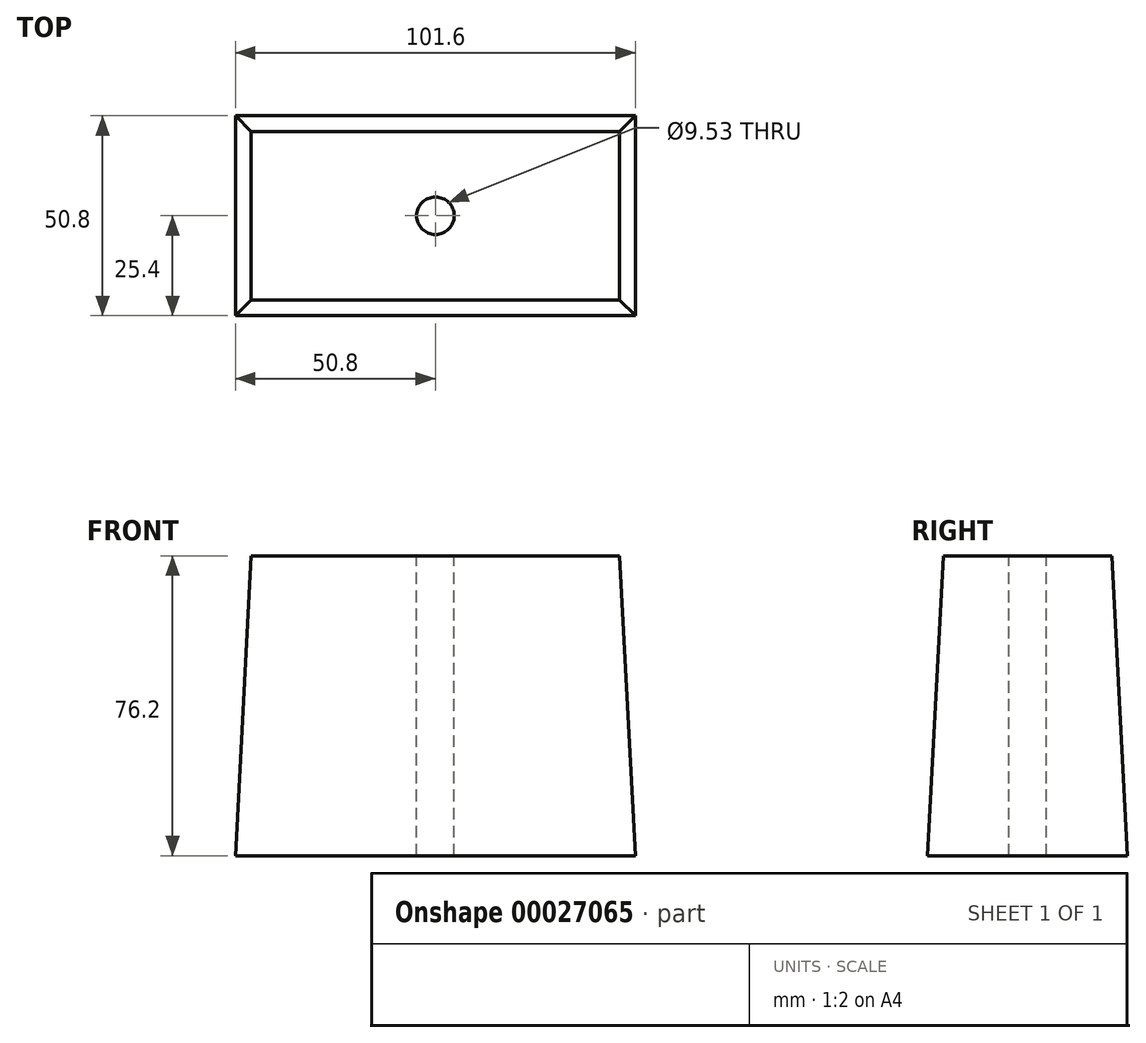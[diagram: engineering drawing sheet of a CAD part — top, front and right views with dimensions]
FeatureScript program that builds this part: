
annotation { "Feature Type Name" : "Feature", "Feature Type Description" : "" }
export const myFeature = defineFeature(function(context is Context, id is Id, definition is map)
    precondition{}
    {
        {
            var Q0;
            Q0=qCreatedBy(makeId("Top.planeOp"),FACE);
            var sketch = newSketch(context, id + "F0", { "sketchPlane" : qUnion([Q0])});
            skLineSegment(sketch, "E0.bottom", {"start": v(0, 0) * mm, "end": v(101.6, 0) * mm});
            skLineSegment(sketch, "E0.top", {"start": v(0, -50.8) * mm, "end": v(101.6, -50.8) * mm});
            skLineSegment(sketch, "E0.left", {"start": v(0, 0) * mm, "end": v(0, -50.8) * mm});
            skLineSegment(sketch, "E0.right", {"start": v(101.6, 0) * mm, "end": v(101.6, -50.8) * mm});
            skSolve(sketch);
        }
        {
            var Q0;
            Q0 = qSketchRegion(id + "F0", true);
            extrude(context, id + "F1", {"entities" : qUnion([Q0]), "depth" : 76.2 * mm, "hasDraft" : true, "draftAngle" : 3 * degree, "draftPullDirection" : true});
        }
        {
            var Q0;
            Q0=makeQuery(id+"F1.opExtrude","CAP_FACE",FACE,{"disambiguationData":[OSD([sQuery(id+"F0.wireOp",EDGE,"E0.bottom"),sQuery(id+"F0.wireOp",EDGE,"E0.top"),sQuery(id+"F0.wireOp",EDGE,"E0.left"),sQuery(id+"F0.wireOp",EDGE,"E0.right")])],"isStart":false});
            var sketch = newSketch(context, id + "F2", { "sketchPlane" : qUnion([Q0])});
            skLineSegment(sketch, "E1", {"start": v(4, -4) * mm, "end": v(97.6, -46.8) * mm, "construction": true});
            skCircle(sketch, "E2", {"center": v(50.8, -25.4) * mm, "radius": 4.76 * mm});
            skSolve(sketch);
        }
        {
            var Q0;
            Q0 = qSketchRegion(id + "F2", true);
            extrude(context, id + "F3", {"entities" : qUnion([Q0]), "operationType" : NewBodyOperationType.REMOVE, "endBound" : BoundingType.THROUGH_ALL, "oppositeDirection" : true, "depth" : 25.4 * mm});
        }
    });
